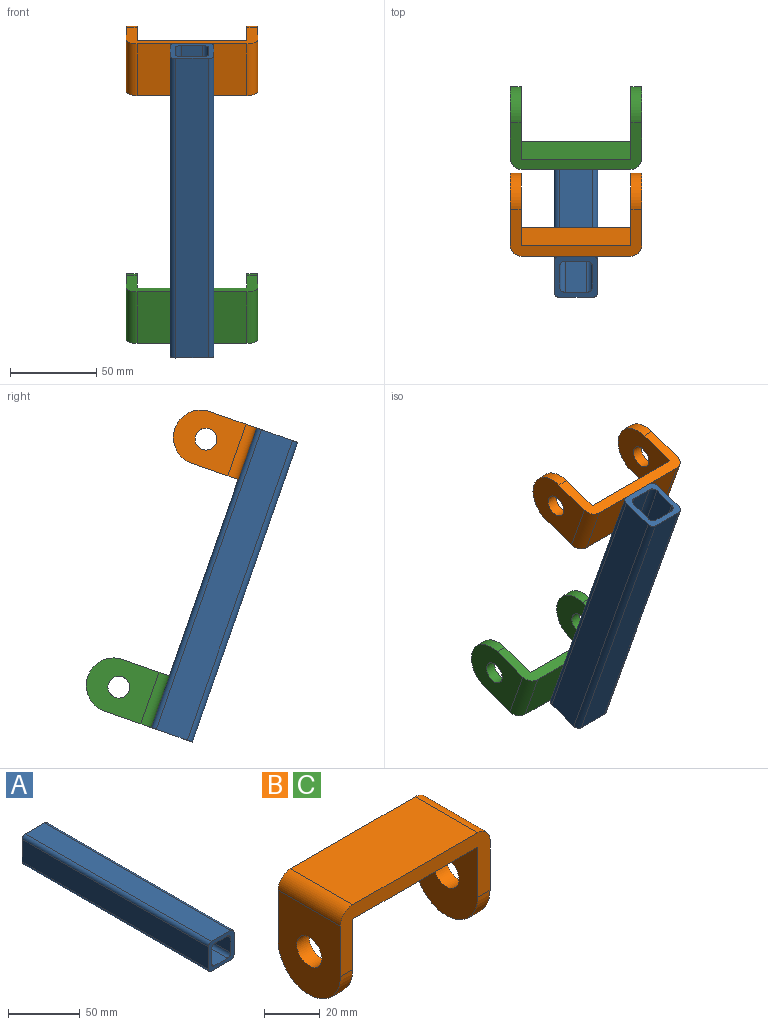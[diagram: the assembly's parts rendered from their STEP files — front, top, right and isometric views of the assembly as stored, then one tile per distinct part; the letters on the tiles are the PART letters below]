
ASSEMBLY  parts=3 mates=2
PART A: 18 faces, bbox 25.4x184.2x25.4 mm
  f0: cylinder r=3.17mm len=184.15mm, axis (0,1,0), area 918.4mm2, adj f1,f15,f16,f17
  f1: plane 184.15x19.05mm, normal (0,0,1), area 3508.1mm2, adj f0,f2,f16,f17
  f2: cylinder r=3.17mm len=184.15mm, axis (0,1,0), area 918.4mm2, adj f1,f3,f16,f17
  f3: plane 184.15x19.05mm, normal (-1,0,0), area 3508.1mm2, adj f2,f4,f16,f17
  f4: cylinder r=3.17mm len=184.15mm, axis (0,1,0), area 918.4mm2, adj f3,f5,f16,f17
  f5: plane 184.15x19.05mm, normal (0,0,-1), area 3508.1mm2, adj f4,f6,f16,f17
  f6: cylinder r=3.17mm len=184.15mm, axis (0,1,0), area 918.4mm2, adj f5,f15,f16,f17
  f7: plane 184.15x12.7mm, normal (0,0,-1), area 2338.7mm2, adj f8,f14,f16,f17
  f8: cylinder r=3.17mm len=184.15mm, axis (0,1,0), area 918.4mm2, adj f7,f9,f16,f17
  f9: plane 184.15x12.7mm, normal (-1,0,0), area 2338.7mm2, adj f8,f10,f16,f17
  f10: cylinder r=3.17mm len=184.15mm, axis (0,1,0), area 918.4mm2, adj f9,f11,f16,f17
  f11: plane 184.15x12.7mm, normal (0,0,1), area 2338.7mm2, adj f10,f12,f16,f17
  f12: cylinder r=3.17mm len=184.15mm, axis (0,1,0), area 918.4mm2, adj f11,f13,f16,f17
  f13: plane 184.15x12.7mm, normal (1,0,0), area 2338.7mm2, adj f12,f14,f16,f17
  f14: cylinder r=3.17mm len=184.15mm, axis (0,1,0), area 918.4mm2, adj f7,f13,f16,f17
  f15: plane 184.15x19.05mm, normal (1,0,0), area 3508.1mm2, adj f0,f6,f16,f17
  f16: plane 25.4x25.4mm, normal (0,-1,0), area 282.3mm2, adj f0,f1,f2,f3,f4,f5,f6,f7
  f17: plane 25.4x25.4mm, normal (0,1,0), area 282.3mm2, adj f0,f1,f2,f3,f4,f5,f6,f7
PART B: 14 faces, bbox 76.2x31.8x44.5 mm
  f0: plane 38.1x31.75mm, normal (1,0,0), area 974.8mm2, adj f2,f3,f9,f11,f13
  f1: plane 38.1x31.75mm, normal (-1,0,0), area 974.8mm2, adj f2,f3,f8,f10,f12
  f2: plane 76.2x28.58mm, normal (0,-1,0), area 748.8mm2, adj f0,f1,f4,f5,f6,f7,f10,f11
  f3: plane 76.2x28.58mm, normal (0,1,0), area 748.8mm2, adj f0,f1,f4,f5,f6,f7,f10,f11
  f4: plane 63.5x31.75mm, normal (0,0,1), area 2016.1mm2, adj f2,f3,f12,f13
  f5: plane 38.1x31.75mm, normal (-1,0,0), area 974.8mm2, adj f2,f3,f6,f9,f11
  f6: plane 63.5x31.75mm, normal (0,0,-1), area 2016.1mm2, adj f2,f3,f5,f7
  f7: plane 38.1x31.75mm, normal (1,0,0), area 974.8mm2, adj f2,f3,f6,f8,f10
  f8: cylinder r=6.35mm len=12.7mm, axis (1,0,0), area 253.4mm2, adj f1,f7
  f9: cylinder r=6.35mm len=12.7mm, axis (1,0,0), area 253.4mm2, adj f0,f5
  f10: cylinder r=15.88mm len=31.75mm, axis (1,0,0), area 316.7mm2, adj f1,f2,f3,f7
  f11: cylinder r=15.88mm len=31.75mm, axis (1,0,0), area 316.7mm2, adj f0,f2,f3,f5
  f12: cylinder r=6.35mm len=31.75mm, axis (0,-1,0), area 316.7mm2, adj f1,f2,f3,f4
  f13: cylinder r=6.35mm len=31.75mm, axis (0,-1,0), area 316.7mm2, adj f0,f2,f3,f4
PART C: same geometry as B
PLACE A rot(axis=(-0.5,-0.71,0.5),109.5deg) t=(141.82,29.02,-183.82)mm
PLACE B rot(axis=(1,0,0),109.4deg) t=(179.83,-14.58,-3.95)mm
PLACE C rot(axis=(1,0,0),109.4deg) t=(179.83,35.93,-147.74)mm
MATE fastened C.f4 <-> A.f15  axis (0,-0.94,-0.33) through (141.73,40.46,-179.8)mm
MATE fastened A.f15 <-> B.f4  axis (0,0.94,0.33) through (141.73,-20.57,-6.06)mm
